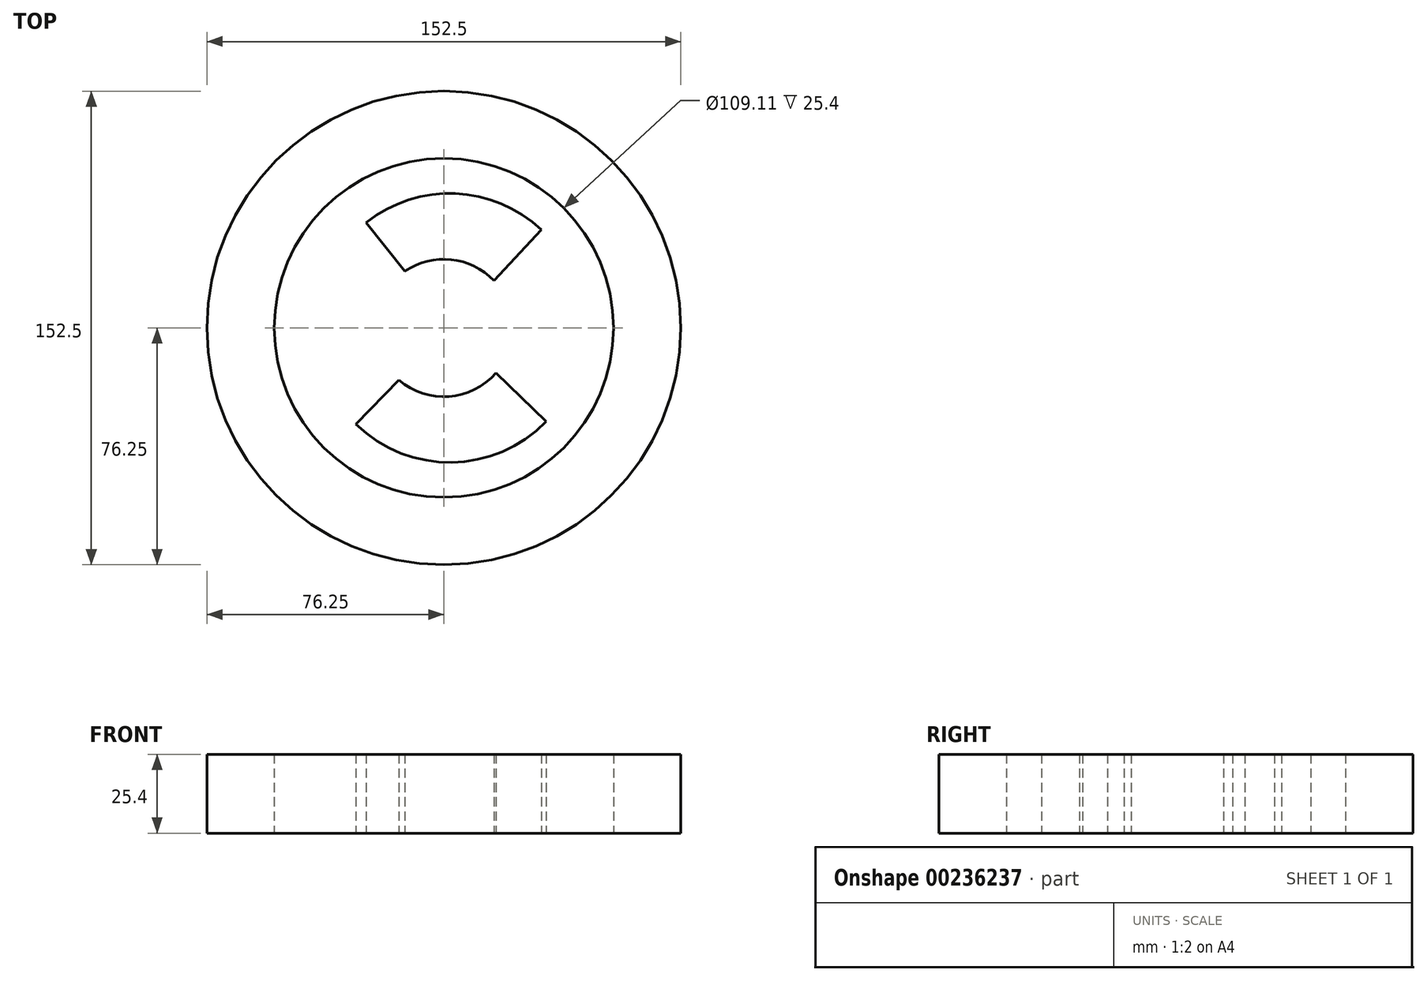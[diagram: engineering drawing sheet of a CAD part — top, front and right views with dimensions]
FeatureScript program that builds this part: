
annotation { "Feature Type Name" : "Feature", "Feature Type Description" : "" }
export const myFeature = defineFeature(function(context is Context, id is Id, definition is map)
    precondition{}
    {
        {
            var Q0;
            Q0=qCreatedBy(makeId("Top.planeOp"),FACE);
            var sketch = newSketch(context, id + "F0", { "sketchPlane" : qUnion([Q0])});
            skCircle(sketch, "E0", {"center": v(0, 0) * mm, "radius": 76.25 * mm});
            skCircle(sketch, "E1", {"center": v(0, 0) * mm, "radius": 54.56 * mm});
            skCircle(sketch, "E2", {"center": v(0, 0) * mm, "radius": 26.77 * mm});
            skLineSegment(sketch, "E3", {"start": v(0, 0) * mm, "end": v(-17.14, 20.56) * mm});
            skLineSegment(sketch, "E4", {"start": v(0, 0) * mm, "end": v(-20.56, -17.14) * mm});
            skLineSegment(sketch, "E5", {"start": v(0, 0) * mm, "end": v(19.81, -18) * mm});
            skLineSegment(sketch, "E6", {"start": v(0, 0) * mm, "end": v(19.24, 18.61) * mm});
            skSolve(sketch);
        }
        {
            var Q0;
            Q0=makeQuery(id+"F0.imprint","IMPRINT",FACE,{"disambiguationData":[TD([[makeQuery(id+"F0.imprint","IMPRINT",EDGE,{"derivedFrom":sQuery(id+"F0.wireOp",EDGE,"E0")}),1.0]])]});
            extrude(context, id + "F1", {"entities" : qUnion([Q0]), "depth" : 25.4 * mm});
        }
        {
            var Q0;
            Q0=qCreatedBy(makeId("Top.planeOp"),FACE);
            var sketch = newSketch(context, id + "F2", { "sketchPlane" : qUnion([Q0])});
            skLineSegment(sketch, "E7", {"start": v(-76.06, 0) * mm, "end": v(76.37, 0) * mm});
            skLineSegment(sketch, "E8", {"start": v(0, -76.62) * mm, "end": v(0, 76.55) * mm});
            skCircle(sketch, "E9", {"center": v(1.87, 0) * mm, "radius": 43.28 * mm});
            skCircle(sketch, "E10", {"center": v(0, 0) * mm, "radius": 22.14 * mm});
            skLineSegment(sketch, "E11", {"start": v(1.87, 0) * mm, "end": v(-52.21, -55.72) * mm});
            skLineSegment(sketch, "E12", {"start": v(1.87, 0) * mm, "end": v(53.26, 54.92) * mm});
            skLineSegment(sketch, "E13", {"start": v(1.87, 0) * mm, "end": v(-45.82, 60.33) * mm});
            skLineSegment(sketch, "E14", {"start": v(1.87, 0) * mm, "end": v(55.59, -52.14) * mm});
            skSolve(sketch);
        }
        {
            var Q0;
            {var subQ0=sQuery(id+"F2.wireOp",EDGE,"E9");var subQ1=sQuery(id+"F2.wireOp",EDGE,"E8");var subQ2=makeQuery(id+"F2.imprint","INTERSECT",VERTEX,{"disambiguationData":[OD(1.0)],"derivedFrom":[subQ1,subQ0]});Q0=makeQuery(id+"F2.imprint","IMPRINT",FACE,{"disambiguationData":[TD([[makeQuery(id+"F2.imprint","IMPRINT",EDGE,{"disambiguationData":[TD([[subQ2,1.0]])],"derivedFrom":subQ1}),1.0]])]});}
            var Q1;
            {var subQ0=sQuery(id+"F2.wireOp",EDGE,"E9");var subQ1=sQuery(id+"F2.wireOp",EDGE,"E8");var subQ2=makeQuery(id+"F2.imprint","INTERSECT",VERTEX,{"disambiguationData":[OD(1.0)],"derivedFrom":[subQ1,subQ0]});Q1=makeQuery(id+"F2.imprint","IMPRINT",FACE,{"disambiguationData":[TD([[makeQuery(id+"F2.imprint","IMPRINT",EDGE,{"disambiguationData":[TD([[subQ2,1.0]])],"derivedFrom":subQ1}),-1.0]])]});}
            var Q2;
            {var subQ0=sQuery(id+"F2.wireOp",EDGE,"E9");var subQ1=sQuery(id+"F2.wireOp",EDGE,"E7");var subQ2=makeQuery(id+"F2.imprint","INTERSECT",VERTEX,{"disambiguationData":[OD(1.0)],"derivedFrom":[subQ1,subQ0]});Q2=makeQuery(id+"F2.imprint","IMPRINT",FACE,{"disambiguationData":[TD([[makeQuery(id+"F2.imprint","IMPRINT",EDGE,{"disambiguationData":[TD([[subQ2,1.0]])],"derivedFrom":subQ1}),1.0]])]});}
            var Q3;
            {var subQ0=sQuery(id+"F2.wireOp",EDGE,"E9");var subQ1=sQuery(id+"F2.wireOp",EDGE,"E7");var subQ2=makeQuery(id+"F2.imprint","INTERSECT",VERTEX,{"disambiguationData":[OD(1.0)],"derivedFrom":[subQ1,subQ0]});Q3=makeQuery(id+"F2.imprint","IMPRINT",FACE,{"disambiguationData":[TD([[makeQuery(id+"F2.imprint","IMPRINT",EDGE,{"disambiguationData":[TD([[subQ2,1.0]])],"derivedFrom":subQ1}),-1.0]])]});}
            var Q4;
            {var subQ0=sQuery(id+"F2.wireOp",EDGE,"E9");var subQ1=sQuery(id+"F2.wireOp",EDGE,"E8");var subQ2=makeQuery(id+"F2.imprint","INTERSECT",VERTEX,{"disambiguationData":[OD(0.0)],"derivedFrom":[subQ1,subQ0]});Q4=makeQuery(id+"F2.imprint","IMPRINT",FACE,{"disambiguationData":[TD([[makeQuery(id+"F2.imprint","IMPRINT",EDGE,{"disambiguationData":[TD([[subQ2,-1.0]])],"derivedFrom":subQ1}),-1.0]])]});}
            var Q5;
            {var subQ0=sQuery(id+"F2.wireOp",EDGE,"E9");var subQ1=sQuery(id+"F2.wireOp",EDGE,"E8");var subQ2=makeQuery(id+"F2.imprint","INTERSECT",VERTEX,{"disambiguationData":[OD(0.0)],"derivedFrom":[subQ1,subQ0]});Q5=makeQuery(id+"F2.imprint","IMPRINT",FACE,{"disambiguationData":[TD([[makeQuery(id+"F2.imprint","IMPRINT",EDGE,{"disambiguationData":[TD([[subQ2,-1.0]])],"derivedFrom":subQ1}),1.0]])]});}
            var Q6;
            {var subQ0=sQuery(id+"F2.wireOp",EDGE,"E9");var subQ1=sQuery(id+"F2.wireOp",EDGE,"E7");var subQ2=makeQuery(id+"F2.imprint","INTERSECT",VERTEX,{"disambiguationData":[OD(0.0)],"derivedFrom":[subQ1,subQ0]});Q6=makeQuery(id+"F2.imprint","IMPRINT",FACE,{"disambiguationData":[TD([[makeQuery(id+"F2.imprint","IMPRINT",EDGE,{"disambiguationData":[TD([[subQ2,-1.0]])],"derivedFrom":subQ1}),-1.0]])]});}
            var Q7;
            {var subQ0=sQuery(id+"F2.wireOp",EDGE,"E9");var subQ1=sQuery(id+"F2.wireOp",EDGE,"E7");var subQ2=makeQuery(id+"F2.imprint","INTERSECT",VERTEX,{"disambiguationData":[OD(0.0)],"derivedFrom":[subQ1,subQ0]});Q7=makeQuery(id+"F2.imprint","IMPRINT",FACE,{"disambiguationData":[TD([[makeQuery(id+"F2.imprint","IMPRINT",EDGE,{"disambiguationData":[TD([[subQ2,-1.0]])],"derivedFrom":subQ1}),1.0]])]});}
            extrude(context, id + "F3", {"entities" : qUnion([Q0, Q1, Q2, Q3, Q4, Q5, Q6, Q7]), "depth" : 25.4 * mm});
        }
    });
